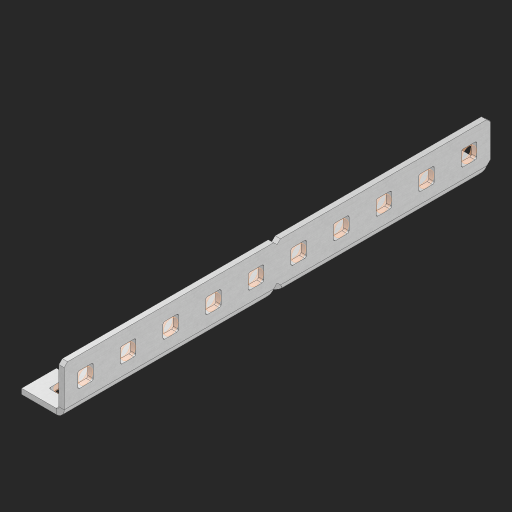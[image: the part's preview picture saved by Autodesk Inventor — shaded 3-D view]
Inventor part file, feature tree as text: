
AUTODESK INVENTOR PART (.ipt)
format: ipt  version: 2023 (Build 270158000, 158)  size: 720,896 bytes
history: native  units: in
note: dims shown in document units (in); Inventor stores cm internally (conversion verified against a paired STEP export)
features: other x178, extrude x28, sheet_metal_op x11, sketch x10, pattern_linear x2, mirror x1, chamfer x1
ambient origin geometry x8: Origin, YZ Plane, XZ Plane, XY Plane, X Axis, Y Axis, Z Axis, Center Point
bodies: Solid1 (feature_tree), Body (feature_tree)
feature tree (231):
  other  "Alu Half C 1x2x1x10"
  other  "Table"
  other  "Alu C 1x2x1x35"
  other  "Alu C 1x2x1x34"
  other  "Alu C 1x2x1x33"
  other  "Alu C 1x2x1x32"
  other  "Alu C 1x2x1x31"
  other  "Alu C 1x2x1x30"
  other  "Alu C 1x2x1x29"
  other  "Alu C 1x2x1x28"
  other  "Alu C 1x2x1x27"
  other  "Alu C 1x2x1x26"
  other  "Alu C 1x2x1x25"
  other  "Alu C 1x2x1x24"
  other  "Alu C 1x2x1x23"
  other  "Alu C 1x2x1x22"
  other  "Alu C 1x2x1x21"
  other  "Alu C 1x2x1x20"
  other  "Alu C 1x2x1x19"
  other  "Alu C 1x2x1x18"
  other  "Alu C 1x2x1x17"
  other  "Alu C 1x2x1x16"
  other  "Alu C 1x2x1x15"
  other  "Alu C 1x2x1x14"
  other  "Alu C 1x2x1x13"
  other  "Alu C 1x2x1x12"
  other  "Alu C 1x2x1x11"
  other  "Alu C 1x2x1x10"
  other  "Alu C 1x2x1x9"
  other  "Alu C 1x2x1x8"
  other  "Alu C 1x2x1x7"
  other  "Alu C 1x2x1x6"
  other  "Alu C 1x2x1x5"
  other  "Alu C 1x2x1x4"
  other  "Alu C 1x2x1x3"
  other  "Alu C 1x2x1x2"
  other  "Alu C 1x2x1x1"
  other  "Steel C 1x2x1x35"
  other  "Steel C 1x2x1x34"
  other  "Steel C 1x2x1x33"
  other  "Steel C 1x2x1x32"
  other  "Steel C 1x2x1x31"
  other  "Steel C 1x2x1x30"
  other  "Steel C 1x2x1x29"
  other  "Steel C 1x2x1x28"
  other  "Steel C 1x2x1x27"
  other  "Steel C 1x2x1x26"
  other  "Steel C 1x2x1x25"
  other  "Steel C 1x2x1x24"
  other  "Steel C 1x2x1x23"
  other  "Steel C 1x2x1x22"
  other  "Steel C 1x2x1x21"
  other  "Steel C 1x2x1x20"
  other  "Steel C 1x2x1x19"
  other  "Steel C 1x2x1x18"
  other  "Steel C 1x2x1x17"
  other  "Steel C 1x2x1x16"
  other  "Steel C 1x2x1x15"
  other  "Steel C 1x2x1x14"
  other  "Steel C 1x2x1x13"
  other  "Steel C 1x2x1x12"
  other  "Steel C 1x2x1x11"
  other  "Steel C 1x2x1x10"
  other  "Steel C 1x2x1x9"
  other  "Steel C 1x2x1x8"
  other  "Steel C 1x2x1x7"
  other  "Steel C 1x2x1x6"
  other  "Steel C 1x2x1x5"
  other  "Steel C 1x2x1x4"
  other  "Steel C 1x2x1x3"
  other  "Steel C 1x2x1x2"
  other  "Steel C 1x2x1x1"
  other  "Alu Half C 1x2x1x35"
  other  "Alu Half C 1x2x1x34"
  other  "Alu Half C 1x2x1x33"
  other  "Alu Half C 1x2x1x32"
  other  "Alu Half C 1x2x1x31"
  other  "Alu Half C 1x2x1x30"
  other  "Alu Half C 1x2x1x29"
  other  "Alu Half C 1x2x1x28"
  other  "Alu Half C 1x2x1x27"
  other  "Alu Half C 1x2x1x26"
  other  "Alu Half C 1x2x1x25"
  other  "Alu Half C 1x2x1x24"
  other  "Alu Half C 1x2x1x23"
  other  "Alu Half C 1x2x1x22"
  other  "Alu Half C 1x2x1x21"
  other  "Alu Half C 1x2x1x20"
  other  "Alu Half C 1x2x1x19"
  other  "Alu Half C 1x2x1x18"
  other  "Alu Half C 1x2x1x17"
  other  "Alu Half C 1x2x1x16"
  other  "Alu Half C 1x2x1x15"
  other  "Alu Half C 1x2x1x14"
  other  "Alu Half C 1x2x1x13"
  other  "Alu Half C 1x2x1x12"
  other  "Alu Half C 1x2x1x11"
  other  "Alu Half C 1x2x1x9"
  other  "Alu Half C 1x2x1x8"
  other  "Alu Half C 1x2x1x7"
  other  "Alu Half C 1x2x1x6"
  other  "Alu Half C 1x2x1x5"
  other  "Alu Half C 1x2x1x4"
  other  "Alu Half C 1x2x1x3"
  other  "Alu Half C 1x2x1x2"
  other  "Alu Half C 1x2x1x1"
  other  "Steel Half C 1x2x1x35"
  other  "Steel Half C 1x2x1x34"
  other  "Steel Half C 1x2x1x33"
  other  "Steel Half C 1x2x1x32"
  other  "Steel Half C 1x2x1x31"
  other  "Steel Half C 1x2x1x30"
  other  "Steel Half C 1x2x1x29"
  other  "Steel Half C 1x2x1x28"
  other  "Steel Half C 1x2x1x27"
  other  "Steel Half C 1x2x1x26"
  other  "Steel Half C 1x2x1x25"
  other  "Steel Half C 1x2x1x24"
  other  "Steel Half C 1x2x1x23"
  other  "Steel Half C 1x2x1x22"
  other  "Steel Half C 1x2x1x21"
  other  "Steel Half C 1x2x1x20"
  other  "Steel Half C 1x2x1x19"
  other  "Steel Half C 1x2x1x18"
  other  "Steel Half C 1x2x1x17"
  other  "Steel Half C 1x2x1x16"
  other  "Steel Half C 1x2x1x15"
  other  "Steel Half C 1x2x1x14"
  other  "Steel Half C 1x2x1x13"
  other  "Steel Half C 1x2x1x12"
  other  "Steel Half C 1x2x1x11"
  other  "Steel Half C 1x2x1x10"
  other  "Steel Half C 1x2x1x9"
  other  "Steel Half C 1x2x1x8"
  other  "Steel Half C 1x2x1x7"
  other  "Steel Half C 1x2x1x6"
  other  "Steel Half C 1x2x1x5"
  other  "Steel Half C 1x2x1x4"
  other  "Steel Half C 1x2x1x3"
  other  "Steel Half C 1x2x1x2"
  other  "Steel Half C 1x2x1x1"
  sheet_metal_op  "Flanges"
  other  "Flange Pattern Plane"
  other  "Flange Pattern Sketch"
  sheet_metal_op  "Flange Pattern"
  sheet_metal_op  "Body Pattern"
  pattern_linear  "Center Pattern"  Spacing1=0.0625in  [1 undecoded]
  other  "Arc Length"
  mirror  "Notch Mirror"
  pattern_linear  "Notch Pattern"  Spacing1=0.182in  [1 undecoded]
  chamfer  "End Chamfer"
  extrude  "Half Cut"  Depth=0.02in
  sketch  "Sketch1"  dims[d0=1.0in]
  other  "Plate1"
  sketch  "Sketch2"  dims[d1=5.0in]
  other  "Plate2"
  sheet_metal_op  "Bend1"
  sheet_metal_op  "Corner1"
  sketch  "Sketch3"  dims[d2=0.0625in]
  sketch  "Sketch7"  dims[d3=0.0625in]
  other  "Srf1"
  other  "Srf2"
  sketch  "Sketch8"  dims[d4=0.0312in]
  sketch  "Sketch9"  dims[d5=0.125in]
  other  "Srf91"
  sheet_metal_op  "Body Pattern Sketch"
  other  "Srf92"
  sketch  "Sketch13"  dims[d6=0.0625in]
  sketch  "Sketch14"  dims[d7=0.5in d8=90.0deg d9=0.0312in]
  sketch  "Sketch15"  dims[d10=0.25in]
  sketch  "Sketch16"  dims[d11=0.0625in d12=0.0625in d16=0.182in d17=0.02in d18=0.0625in d19=0.0in d20=0.25in d21=0.25in d38=3.937in d40=0.5in d41=0.3937in d43=1.0in d46=0.172in d47=1.0in d48=0.0in d49=0.182in d50=0.02in d51=0.25in d52=0.25in d53=0.0625in d54=0.0in d55=0.172in d56=1.0in d57=0.0in d58=0.25in d60=3.937in d62=0.5in d63=0.3937in d65=0.5in d85=0.1473in d86=0.1782in d88=0.04in d89=0.0625in d90=0.0in d91=0.04in d92=0.0491in d95=2.5in d96=0.04in d97=0.25in d98=45.0deg d99=0.25in d100=0.5in d101=0.0in d102=2.497in d106=0.182in d107=0.02in d108=0.5in d109=0.5in d110=0.0625in d111=0.0in d112=0.172in d113=0.5in d114=0.0in d117=0.5in d118=0.5in d119=0.5in]
  other  "Srf786"
  other  "Srf823"
  other  "Srf824"
  other  "Srf825"
  other  "Srf826"
  other  "Srf827"
  other  "Srf828"
  other  "Srf829"
  other  "Srf856"
  other  "Srf857"
  other  "Srf858"
  other  "Srf859"
  other  "Srf860"
  other  "Srf861"
  other  "Srf862"
  other  "Srf889"
  other  "Srf890"
  other  "Srf891"
  other  "Srf892"
  other  "Srf893"
  other  "Srf894"
  other  "Srf895"
  other  "Srf896"
  other  "Srf922"
  other  "Srf959"
  other  "Srf996"
  sheet_metal_op  "Flange Stamp"
  sheet_metal_op  "Flange Circle"
  sheet_metal_op  "Body Stamp"
  sheet_metal_op  "Body Circle"
  other  "Center Stamp"
  other  "Center Circle"
  sheet_metal_op  "Notch"
  extrude  "ExtrusionSrf2"  Depth=0.0625in
  extrude  "ExtrusionSrf92"  TaperAngle=0.0deg  [1 undecoded]
  extrude  "ExtrusionSrf823"  Depth=0.25in
  extrude  "ExtrusionSrf824"  Depth=0.25in
  extrude  "ExtrusionSrf825"  Depth=0.5in
  extrude  "ExtrusionSrf826"  Depth=0.5in
  extrude  "ExtrusionSrf827"  Depth=1.0in TaperAngle=0.0deg
  extrude  "ExtrusionSrf828"  Depth=0.182in
  extrude  "ExtrusionSrf829"  Depth=0.02in
  extrude  "ExtrusionSrf856"  Depth=0.25in
  extrude  "ExtrusionSrf857"  Depth=0.25in
  extrude  "ExtrusionSrf858"  Depth=0.0625in
  extrude  "ExtrusionSrf859"  TaperAngle=0.0deg  [1 undecoded]
  extrude  "ExtrusionSrf860"  Depth=0.5in
  extrude  "ExtrusionSrf861"  Depth=1.0in TaperAngle=0.0deg
  extrude  "ExtrusionSrf862"  Depth=0.25in
  extrude  "ExtrusionSrf889"  Depth=0.5in
  extrude  "ExtrusionSrf890"  Depth=0.5in
  extrude  "ExtrusionSrf891"  Depth=0.5in
  extrude  "ExtrusionSrf892"  Depth=0.5in
  extrude  "ExtrusionSrf893"  Depth=0.5in
  extrude  "ExtrusionSrf894"  Depth=0.0625in
  extrude  "ExtrusionSrf895"  TaperAngle=0.0deg  [1 undecoded]
  extrude  "ExtrusionSrf896"  Depth=0.5in
  extrude  "ExtrusionSrf922"  Depth=0.5in
  extrude  "ExtrusionSrf959"  Depth=2.5in
  extrude  "ExtrusionSrf996"  Depth=0.25in TaperAngle=45.0deg
note: 5 required parameter values undecoded (feature->parameter linkage not recoverable at this tier; creation-order binding heuristic only, values carry confidence <= 0.55)
